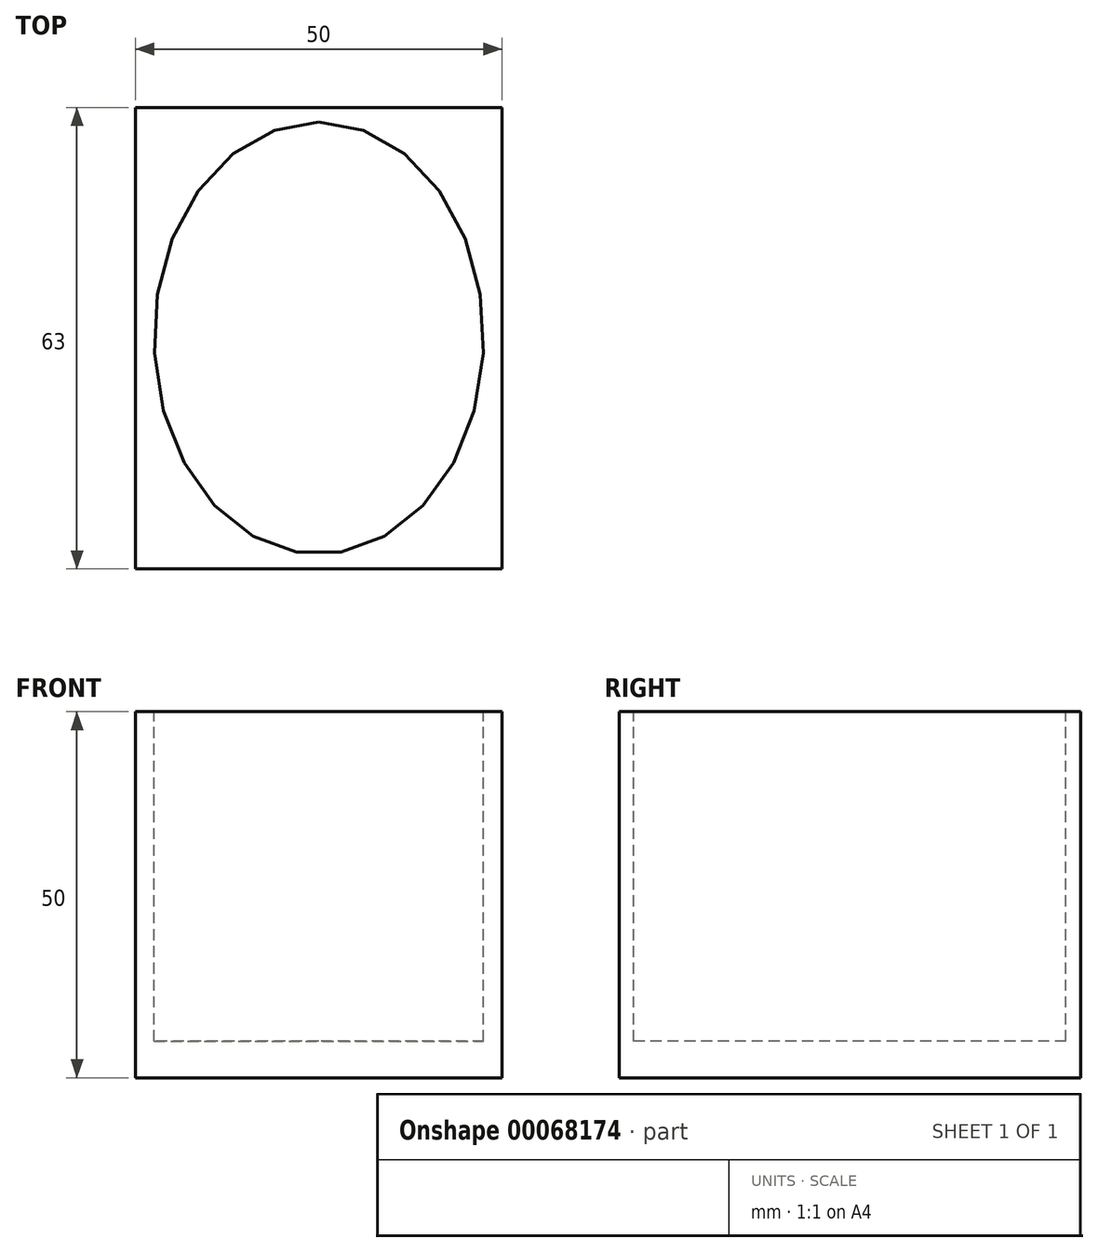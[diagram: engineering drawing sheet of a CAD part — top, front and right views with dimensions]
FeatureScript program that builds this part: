
annotation { "Feature Type Name" : "Feature", "Feature Type Description" : "" }
export const myFeature = defineFeature(function(context is Context, id is Id, definition is map)
    precondition{}
    {
        {
            var Q0;
            Q0=qCreatedBy(makeId("Top.planeOp"),FACE);
            var sketch = newSketch(context, id + "F0", { "sketchPlane" : qUnion([Q0])});
            skLineSegment(sketch, "E0.rect.bottom", {"start": v(25, -31.5) * mm, "end": v(-25, -31.5) * mm});
            skLineSegment(sketch, "E0.rect.top", {"start": v(25, 31.5) * mm, "end": v(-25, 31.5) * mm});
            skLineSegment(sketch, "E0.rect.left", {"start": v(25, -31.5) * mm, "end": v(25, 31.5) * mm});
            skLineSegment(sketch, "E0.rect.right", {"start": v(-25, -31.5) * mm, "end": v(-25, 31.5) * mm});
            skPoint(sketch, "E0.rect.middle", {"position": v(0, 0) * mm});
            skSolve(sketch);
        }
        {
            var Q0;
            Q0=makeQuery(id+"F0.imprint","IMPRINT",FACE,{"disambiguationData":[TD([[makeQuery(id+"F0.imprint","IMPRINT",EDGE,{"derivedFrom":sQuery(id+"F0.wireOp",EDGE,"E0.rect.bottom")}),-1.0]])]});
            extrude(context, id + "F1", {"entities" : qUnion([Q0]), "depth" : 50 * mm});
        }
        {
            var Q0;
            Q0=makeQuery(id+"F1.opExtrude","CAP_FACE",FACE,{"disambiguationData":[OSD([sQuery(id+"F0.wireOp",EDGE,"E0.rect.bottom"),sQuery(id+"F0.wireOp",EDGE,"E0.rect.top"),sQuery(id+"F0.wireOp",EDGE,"E0.rect.left"),sQuery(id+"F0.wireOp",EDGE,"E0.rect.right")])],"isStart":false});
            var sketch = newSketch(context, id + "F2", { "sketchPlane" : qUnion([Q0])});
            skEllipse(sketch, "E1", {"center": v(0, 0) * mm, "majorRadius": 29.5 * mm, "minorRadius": 22.5 * mm, "majorAxis": v(0, 1)});
            skSolve(sketch);
        }
        {
            var Q0;
            Q0=makeQuery(id+"F2.imprint","IMPRINT",FACE,{"disambiguationData":[TD([[makeQuery(id+"F2.imprint","IMPRINT",EDGE,{"derivedFrom":sQuery(id+"F2.wireOp",EDGE,"E1")}),1.0]])]});
            extrude(context, id + "F3", {"entities" : qUnion([Q0]), "operationType" : NewBodyOperationType.REMOVE, "oppositeDirection" : true, "depth" : 45 * mm});
        }
    });
